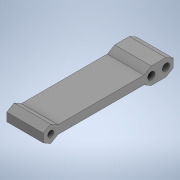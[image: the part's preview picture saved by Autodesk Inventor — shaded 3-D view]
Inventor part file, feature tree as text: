
AUTODESK INVENTOR PART (.ipt)
format: ipt  version: 2020 (Build 240168000, 168)  size: 268,288 bytes
history: native  units: in
note: dims shown in document units (in); Inventor stores cm internally (conversion verified against a paired STEP export)
features: sketch x5, extrude x4, plane x2, projected_geometry x2, mirror x1
ambient origin geometry x8: Origin, YZ Plane, XZ Plane, XY Plane, X Axis, Y Axis, Z Axis, Center Point
bodies: Solid1 (feature_tree)
feature tree (14):
  extrude  "Extrusion1"  Depth=2.7957in
  plane  "Work Plane1"
  extrude  "Extrusion2"  Depth=0.7874in
  sketch  "Sketch4"  dims[d4=0.0in d5=0.0787in]
  extrude  "Extrusion4"  Depth=0.0787in
  plane  "Work Plane2"
  extrude  "Extrusion6"  Depth=2.4807in
  mirror  "Mirror2"
  sketch  "Sketch1"  dims[d0=0.1818in d1=2.7957in]
  sketch  "Sketch2"  dims[d2=0.1299in d3=0.7874in]
  sketch  "Sketch5"  dims[d6=0.7874in d7=0.0in d28=2.4807in]
  sketch  "Sketch7"  dims[d29=0.315in d31=0.315in d33=0.1575in d34=0.2362in d35=0.0in d38=0.315in d39=0.2756in d40=-0.3092in]
  projected_geometry  "Projected Loop7"
  projected_geometry  "Projected Loop8"
